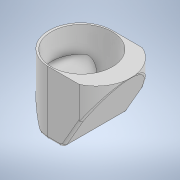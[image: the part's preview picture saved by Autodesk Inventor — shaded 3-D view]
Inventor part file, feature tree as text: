
AUTODESK INVENTOR PART (.ipt)
format: ipt  version: 2020 (Build 240168000, 168)  size: 298,496 bytes
history: native  units: in
note: dims shown in document units (in); Inventor stores cm internally (conversion verified against a paired STEP export)
features: extrude x5, sketch x5, fillet x3
ambient origin geometry x8: Origin, YZ Plane, XZ Plane, XY Plane, X Axis, Y Axis, Z Axis, Center Point
bodies: Solid1 (feature_tree)
feature tree (13):
  extrude  "Extrusion1"  Depth=1.063in
  sketch  "Sketch2"  dims[d2=1.063in d3=0.0in d4=0.0394in]
  extrude  "Extrusion2"  Depth=0.0394in
  extrude  "Extrusion3"  Depth=0.0394in
  extrude  "Extrusion4"  Depth=0.2165in
  extrude  "Extrusion5"  Depth=0.04in
  fillet  "Fillet1"  Radius=1.063in
  fillet  "Fillet2"  Radius=0.4331in
  fillet  "Fillet3"  Radius=1.063in
  sketch  "Sketch1"  dims[d0=1.378in d1=1.063in]
  sketch  "Sketch3"  dims[d5=0.5118in d6=0.0394in]
  sketch  "Sketch4"  dims[d7=0.5118in d8=0.2165in]
  sketch  "Sketch5"  dims[d9=0.2165in d10=0.4331in d11=1.063in d12=0.0in d13=0.4331in d14=0.0in d15=1.063in d16=0.0in d17=0.2165in d18=0.2165in d19=0.6102in d20=0.0in d21=0.3in d22=0.09in d23=0.04in]
